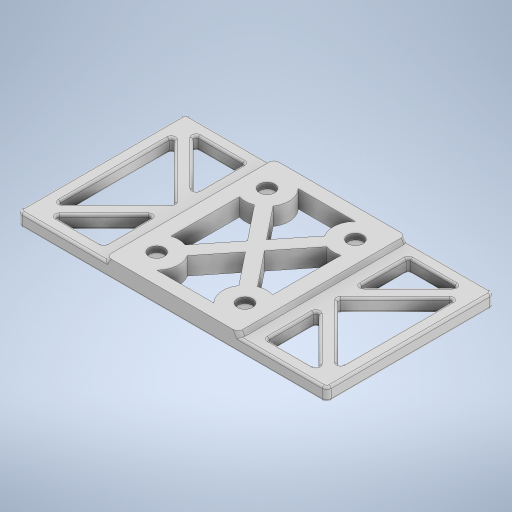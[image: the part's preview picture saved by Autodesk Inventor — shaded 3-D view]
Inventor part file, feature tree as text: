
AUTODESK INVENTOR PART (.ipt)
format: ipt  version: 2024.2 (Build 282272000, 272)  size: 576,000 bytes
history: native  units: mm
features: sketch x7, extrude x6, fillet x3, chamfer x2, hole x1
ambient origin geometry x8: Origin, YZ Plane, XZ Plane, XY Plane, X Axis, Y Axis, Z Axis, Center Point
bodies: Solid1 (feature_tree)
feature tree (19):
  extrude  "Extrusion1"  Depth=38.0mm
  extrude  "Extrusion2"  Depth=1.0mm
  chamfer  "Chamfer2"  Distance=1.0mm
  chamfer  "Chamfer3"  Distance=1.0mm Angle=30.0deg
  extrude  "Extrusion3"  Depth=1.0mm
  fillet  "Fillet1"  Radius=3.0mm
  fillet  "Fillet4"  Radius=3.0mm
  hole  "Hole1"  [1 undecoded]
  extrude  "Extrusion6"  TaperAngle=0.0deg  [1 undecoded]
  fillet  "Fillet3"  Radius=0.5mm
  extrude  "Extrusion4"  Depth=0.5mm
  extrude  "Extrusion5"  Depth=1.5mm
  sketch  "Sketch1"  dims[d0=70.0mm d1=38.0mm]
  sketch  "Sketch2"  dims[d2=3.0mm d3=0.0mm d4=31.0mm d5=1.0mm d6=0.0mm d10=1.0mm d11=2.0mm d12=30.0deg]
  sketch  "Sketch3"  dims[d13=1.0mm d14=2.0mm d15=30.0deg d16=1.0mm d19=3.0mm d20=3.0mm]
  sketch  "Sketch4"  dims[d21=3.0mm d22=3.0mm]
  sketch  "Sketch5"  dims[d24=3.0mm d25=0.0mm d26=0.0mm d27=0.5mm]
  sketch  "Sketch6"  dims[d28=0.5mm d29=3.5mm]
  sketch  "Sketch7"  dims[d30=20.0mm d31=25.0mm d32=45.0mm d33=31.5mm d34=3.5mm d35=6.0mm d36=5.25mm d37=1.0mm d38=90.0deg d39=8.0mm d40=20.594885mm d41=5.6mm d42=2.5mm d43=0.0mm d44=0.2mm d45=0.0mm d46=10.0mm d47=3.0mm d48=3.0mm d49=7.0mm d50=7.0mm d51=3.0mm d52=3.0mm d53=1.5mm d55=1.5mm d56=1.5mm d58=1.5mm d59=0.0mm d60=0.0mm]
note: 2 required parameter values undecoded (feature->parameter linkage not recoverable at this tier; creation-order binding heuristic only, values carry confidence <= 0.55)
